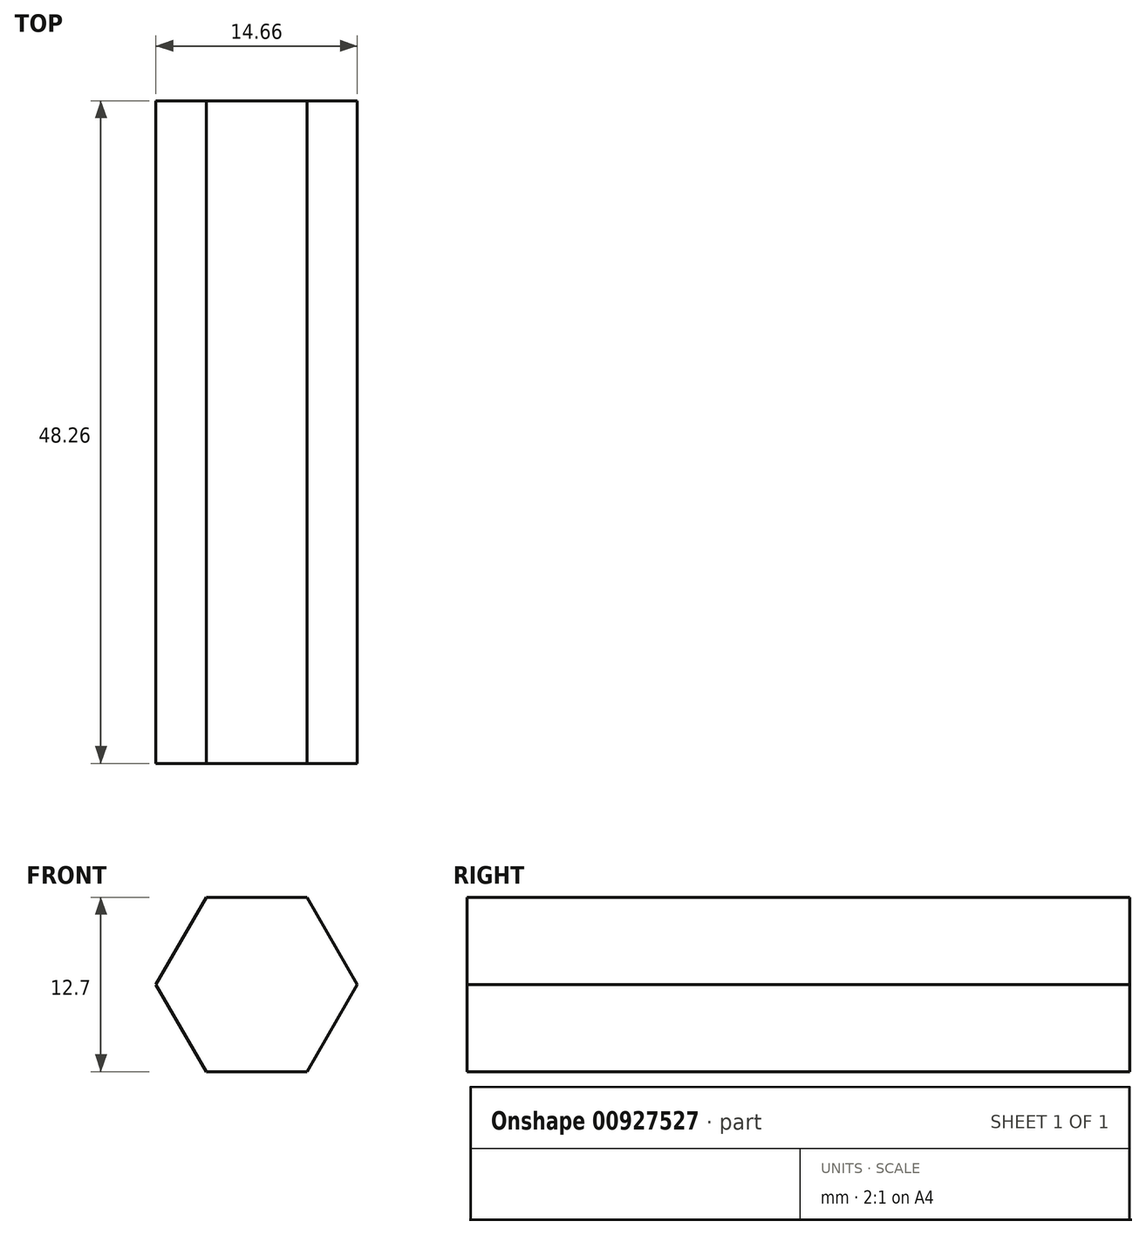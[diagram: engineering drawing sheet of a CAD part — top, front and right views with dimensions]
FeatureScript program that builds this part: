
annotation { "Feature Type Name" : "Feature", "Feature Type Description" : "" }
export const myFeature = defineFeature(function(context is Context, id is Id, definition is map)
    precondition{}
    {
        {
            var Q0;
            Q0=qCreatedBy(makeId("Front.planeOp"),FACE);
            var sketch = newSketch(context, id + "F0", { "sketchPlane" : qUnion([Q0])});
            skCircle(sketch, "E0.cCircle", {"center": v(0, 0) * mm, "radius": 6.35 * mm, "construction": true});
            skLineSegment(sketch, "E0.0", {"start": v(-3.67, 6.35) * mm, "end": v(3.67, 6.35) * mm});
            skLineSegment(sketch, "E0.1", {"start": v(3.67, 6.35) * mm, "end": v(7.33, 0) * mm});
            skLineSegment(sketch, "E0.2", {"start": v(7.33, 0) * mm, "end": v(3.67, -6.35) * mm});
            skLineSegment(sketch, "E0.3", {"start": v(3.67, -6.35) * mm, "end": v(-3.67, -6.35) * mm});
            skLineSegment(sketch, "E0.4", {"start": v(-3.67, -6.35) * mm, "end": v(-7.33, 0) * mm});
            skLineSegment(sketch, "E0.5", {"start": v(-7.33, 0) * mm, "end": v(-3.67, 6.35) * mm});
            skPoint(sketch, "E0.0.midPoint", {"position": v(0, 6.35) * mm});
            skSolve(sketch);
        }
        {
            var Q0;
            Q0=qSketchRegion(id+"F0",true);
            var Q1;
            Q1=makeQuery(id+"F0.imprint","IMPRINT",FACE,{"disambiguationData":[TD([[makeQuery(id+"F0.imprint","IMPRINT",EDGE,{"derivedFrom":sQuery(id+"F0.wireOp",EDGE,"E0.0")}),-1.0]])]});
            extrude(context, id + "F1", {"entities" : qUnion([Q0, Q1]), "depth" : 48.26 * mm, "offsetDistance" : 25.4 * mm});
        }
    });
